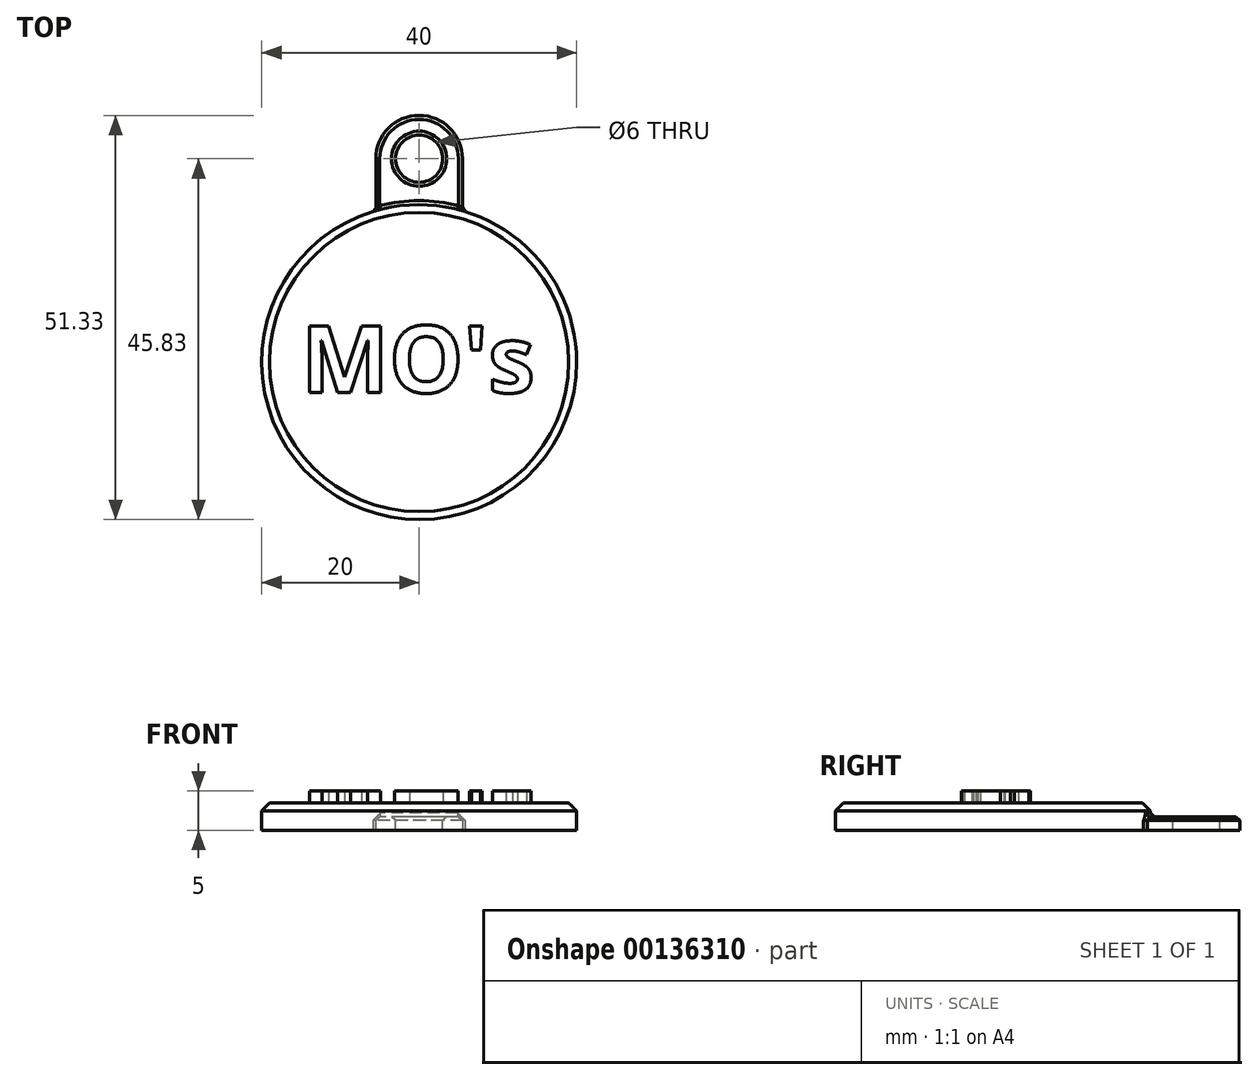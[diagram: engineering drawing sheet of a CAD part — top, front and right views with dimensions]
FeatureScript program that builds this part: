
annotation { "Feature Type Name" : "Feature", "Feature Type Description" : "" }
export const myFeature = defineFeature(function(context is Context, id is Id, definition is map)
    precondition{}
    {
        {
            var Q0;
            Q0=qCreatedBy(makeId("Top.planeOp"),FACE);
            var sketch = newSketch(context, id + "F0", { "sketchPlane" : qUnion([Q0])});
            skCircle(sketch, "E0", {"center": v(0, 0) * mm, "radius": 20 * mm});
            skCircle(sketch, "E1", {"center": v(0, 25.83) * mm, "radius": 3 * mm});
            skArc(sketch, "E2.0", {"start": v(5.5, 25.83) * mm, "mid": v(0, 31.33) * mm, "end": v(-5.5, 25.83) * mm});
            skLineSegment(sketch, "E3", {"start": v(-5.5, 25.83) * mm, "end": v(-5.5, 19.23) * mm});
            skLineSegment(sketch, "E4", {"start": v(5.5, 25.83) * mm, "end": v(5.5, 19.23) * mm});
            skSolve(sketch);
        }
        {
            var Q0;
            {var subQ0=sQuery(id+"F0.wireOp",EDGE,"E0");var subQ1=makeQuery(id+"F0.imprint","INTERSECT",VERTEX,{"derivedFrom":[subQ0,sQuery(id+"F0.wireOp",EDGE,"E3")]});Q0=makeQuery(id+"F0.imprint","IMPRINT",FACE,{"disambiguationData":[TD([[makeQuery(id+"F0.imprint","IMPRINT",EDGE,{"disambiguationData":[TD([[subQ1,1.0]])],"derivedFrom":subQ0}),1.0]])]});}
            extrude(context, id + "F1", {"entities" : qUnion([Q0]), "endBound" : BoundingType.SYMMETRIC, "depth" : 3.5 * mm});
        }
        {
            var Q0;
            Q0=makeQuery(id+"F0.imprint","IMPRINT",FACE,{"disambiguationData":[TD([[makeQuery(id+"F0.imprint","IMPRINT",EDGE,{"derivedFrom":sQuery(id+"F0.wireOp",EDGE,"E1")}),-1.0]])]});
            var Q1;
            Q1=makeQuery(id+"F1.opExtrude","CAP_FACE",FACE,{"disambiguationData":[OSD([sQuery(id+"F0.wireOp",EDGE,"E0")])],"isStart":true});
            extrude(context, id + "F2", {"entities" : qUnion([Q0]), "operationType" : NewBodyOperationType.ADD, "endBound" : BoundingType.UP_TO_SURFACE, "oppositeDirection" : true, "endBoundEntityFace" : qUnion([Q1]), "depth" : 2 * mm});
        }
        {
            var Q0;
            Q0=makeQuery(id+"F1.opExtrude","CAP_EDGE",EDGE,{"disambiguationData":[OSD([sQuery(id+"F0.wireOp",EDGE,"E0")])],"isStart":false});
            chamfer(context, id + "F3", {"entities" : qUnion([Q0]), "width" : 1 * mm, "tangentPropagation" : true});
        }
        {
            var Q0;
            Q0=makeQuery(id+"F1.opExtrude","CAP_FACE",FACE,{"disambiguationData":[OSD([sQuery(id+"F0.wireOp",EDGE,"E0")])],"isStart":false});
            var sketch = newSketch(context, id + "F4", { "sketchPlane" : qUnion([Q0])});
            skText(sketch, "E5", { "text": "MO\'s", "fontName": "OpenSans-Bold.ttf"});
            skLineSegment(sketch, "E6", {"start": v(0, 19) * mm, "end": v(0, -19) * mm, "construction": true});
            const initialGuessF4  = {"E5": [-0.015, -0.00388, 1, 0, 0.00854]};
            skSetInitialGuess(sketch, initialGuessF4);
            skSolve(sketch);
        }
        {
            var Q0;
            Q0=qSketchRegion(id+"F4",true);
            extrude(context, id + "F5", {"entities" : qUnion([Q0]), "operationType" : NewBodyOperationType.ADD, "depth" : 1.5 * mm});
        }
        {
            var Q0;
            Q0=makeQuery(id+"F2.opExtrude","CAP_FACE",FACE,{"disambiguationData":[OSD([sQuery(id+"F0.wireOp",EDGE,"E0"),sQuery(id+"F0.wireOp",EDGE,"E1"),sQuery(id+"F0.wireOp",EDGE,"E2.0"),sQuery(id+"F0.wireOp",EDGE,"E3"),sQuery(id+"F0.wireOp",EDGE,"E4")])],"isStart":true});
            chamfer(context, id + "F6", {"entities" : qUnion([Q0]), "width" : .5 * mm, "tangentPropagation" : true});
        }
    });
